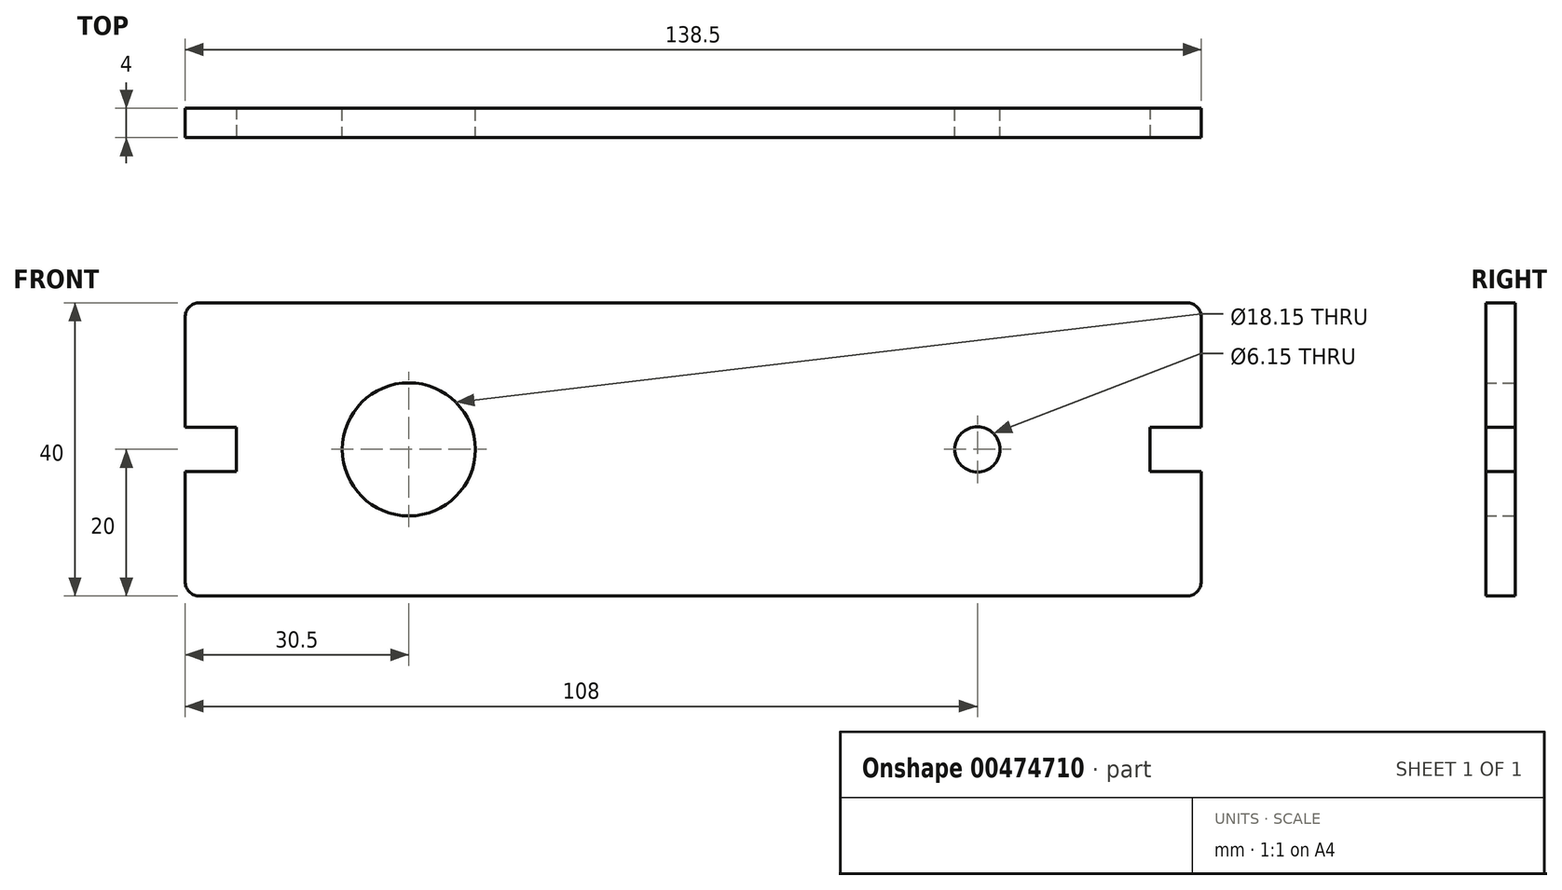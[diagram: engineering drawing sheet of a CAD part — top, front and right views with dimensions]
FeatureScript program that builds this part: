
annotation { "Feature Type Name" : "Feature", "Feature Type Description" : "" }
export const myFeature = defineFeature(function(context is Context, id is Id, definition is map)
    precondition{}
    {
        {
            var Q0;
            Q0=qCreatedBy(makeId("Front.planeOp"),FACE);
            var sketch = newSketch(context, id + "F0", { "sketchPlane" : qUnion([Q0])});
            skLineSegment(sketch, "E0.bottom", {"start": v(69.25, 20) * mm, "end": v(-69.25, 20) * mm});
            skLineSegment(sketch, "E0.top", {"start": v(69.25, -20) * mm, "end": v(-69.25, -20) * mm});
            skLineSegment(sketch, "E0.left", {"start": v(69.25, 20) * mm, "end": v(69.25, -20) * mm});
            skLineSegment(sketch, "E0.right", {"start": v(-69.25, 20) * mm, "end": v(-69.25, -20) * mm});
            skPoint(sketch, "E0.middle", {"position": v(0, 0) * mm});
            skCircle(sketch, "E1", {"center": v(-38.75, 0) * mm, "radius": 9.07 * mm});
            skCircle(sketch, "E2", {"center": v(38.75, 0) * mm, "radius": 3.08 * mm});
            skSolve(sketch);
        }
        {
            var Q0;
            Q0=makeQuery(id+"F0.imprint","IMPRINT",FACE,{"disambiguationData":[TD([[makeQuery(id+"F0.imprint","IMPRINT",EDGE,{"derivedFrom":sQuery(id+"F0.wireOp",EDGE,"E0.bottom")}),1.0]])]});
            extrude(context, id + "F1", {"entities" : qUnion([Q0]), "depth" : 4 * mm});
        }
        {
            var Q0;
            Q0=makeQuery(id+"F1.opExtrude","SWEPT_EDGE",EDGE,{"disambiguationData":[OSD([sQuery(id+"F0.wireOp",EDGE,"E0.top"),sQuery(id+"F0.wireOp",EDGE,"E0.right")])]});
            var Q1;
            Q1=makeQuery(id+"F1.opExtrude","SWEPT_EDGE",EDGE,{"disambiguationData":[OSD([sQuery(id+"F0.wireOp",EDGE,"E0.bottom"),sQuery(id+"F0.wireOp",EDGE,"E0.right")])]});
            var Q2;
            Q2=makeQuery(id+"F1.opExtrude","SWEPT_EDGE",EDGE,{"disambiguationData":[OSD([sQuery(id+"F0.wireOp",EDGE,"E0.top"),sQuery(id+"F0.wireOp",EDGE,"E0.left")])]});
            var Q3;
            Q3=makeQuery(id+"F1.opExtrude","SWEPT_EDGE",EDGE,{"disambiguationData":[OSD([sQuery(id+"F0.wireOp",EDGE,"E0.bottom"),sQuery(id+"F0.wireOp",EDGE,"E0.left")])]});
            fillet(context, id + "F2", {"entities" : qUnion([Q0, Q1, Q2, Q3]), "radius" : 2 * mm, "tangentPropagation" : true, "allowEdgeOverflow" : false});
        }
        {
            var Q0;
            Q0=makeQuery(id+"F1.opExtrude","CAP_FACE",FACE,{"disambiguationData":[OSD([sQuery(id+"F0.wireOp",EDGE,"E0.bottom"),sQuery(id+"F0.wireOp",EDGE,"E0.top"),sQuery(id+"F0.wireOp",EDGE,"E0.left"),sQuery(id+"F0.wireOp",EDGE,"E0.right"),sQuery(id+"F0.wireOp",EDGE,"E1"),sQuery(id+"F0.wireOp",EDGE,"E2")])],"isStart":false});
            var sketch = newSketch(context, id + "F3", { "sketchPlane" : qUnion([Q0])});
            skLineSegment(sketch, "E3.bottom", {"start": v(-62.25, 3.02) * mm, "end": v(-76.25, 3.02) * mm});
            skLineSegment(sketch, "E3.top", {"start": v(-62.25, -3.03) * mm, "end": v(-76.25, -3.03) * mm});
            skLineSegment(sketch, "E3.left", {"start": v(-62.25, 3.02) * mm, "end": v(-62.25, -3.03) * mm});
            skLineSegment(sketch, "E3.right", {"start": v(-76.25, 3.02) * mm, "end": v(-76.25, -3.03) * mm});
            skPoint(sketch, "E3.middle", {"position": v(-69.25, 0) * mm});
            skLineSegment(sketch, "E4.MirrorCS", {"start": v(62.25, 3.02) * mm, "end": v(76.25, 3.02) * mm});
            skLineSegment(sketch, "E5.MirrorCS", {"start": v(62.25, -3.03) * mm, "end": v(76.25, -3.03) * mm});
            skLineSegment(sketch, "E6.MirrorCS", {"start": v(76.25, 3.02) * mm, "end": v(76.25, -3.03) * mm});
            skLineSegment(sketch, "E7.MirrorCS", {"start": v(62.25, 3.02) * mm, "end": v(62.25, -3.03) * mm});
            skPoint(sketch, "E8.MirrorP", {"position": v(69.25, 0) * mm});
            skSolve(sketch);
        }
        {
            var Q0;
            {var subQ0=sQuery(id+"F3.wireOp",EDGE,"E3.left");Q0=makeQuery(id+"F3.imprint","IMPRINT",FACE,{"disambiguationData":[TD([[makeQuery(id+"F3.imprint","IMPRINT",EDGE,{"derivedFrom":subQ0}),-1.0]])]});}
            var Q1;
            {var subQ0=sQuery(id+"F3.wireOp",EDGE,"E7.MirrorCS");Q1=makeQuery(id+"F3.imprint","IMPRINT",FACE,{"disambiguationData":[TD([[makeQuery(id+"F3.imprint","IMPRINT",EDGE,{"derivedFrom":subQ0}),1.0]])]});}
            extrude(context, id + "F4", {"entities" : qUnion([Q0, Q1]), "operationType" : NewBodyOperationType.REMOVE, "oppositeDirection" : true, "depth" : 25 * mm});
        }
    });
